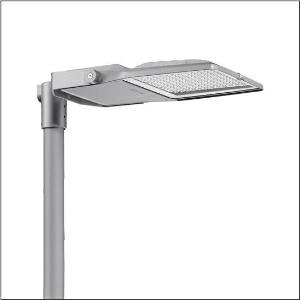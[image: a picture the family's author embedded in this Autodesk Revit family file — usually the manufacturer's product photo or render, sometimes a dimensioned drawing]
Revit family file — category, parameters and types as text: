
# Revit family: floodlight_fl_21_midi___pl43_5xa7786f2a3a_0f3f
name_source: partatom
category: Lighting Fixtures
units: mm (PartAtom-declared; Revit-internal decimal feet)

## family parameters
Cut with Voids When Loaded = No
Host = Face
Light Source = No
Part Type = Normal
Room Calculation Point = No
Round Connector Dimension = Use Diameter
Shared = No

## types (1)
- --- (1 x LED, 36680 lm, 271.6 W, 3000K)
    Apparent Load = 272 VA
    CIE Flux Codes = 27 78 99 100 100
    Color Rendering = 70
    Color Temperature = 3000K
    Default Elevation = 1800 mm
    Description = Floodlight FL 21 midi, floodlight, primary light control with lens, of PMMA, primary optical cover: protective disc, of toughened safety glass, transparent, light distribution: PL43, light emission: direct distribution, installation type: surface-mounted, LED, High Power LED, rated luminous flux: 36.680lm, luminous efficacy: 135lm/W, light colour: 730, colour temperature: 3000K, control gear: ECG Smart Interface, control: flexible luminous flux parameterisation, time-dependent luminous flux control, constant luminous flux control, overheat protection, presetting dimming logarithmic, with terminal, 6-pole, mains connection: 220..240V, AC, 50/60Hz, start of lifetime: 272W, end of service life: 287W, reduction: 123W, luminaire housing, of diecast aluminium, powder-coated, Siteco® metallic grey (DB 702S), corrosivity category C5 mid according to DIN EN ISO 12944, sealing non-destructively replaceable, please order mast flange separately, mast bracket, of steel, galvanised, powder-coated, Siteco® metallic grey (DB 702S), Smart Interface below and above, protection rating (complete): IP66, insulation class (complete): insulation class II (safety insulation), certification: CE, protection symbol: D, impact resistance: IK08, permissible operating ambient temperature: -40..+40°C, permissible operating ambient temperature for outdoor applications: -40..+50°C, standard: DIN EN 12944, LABS conformity tested according to VDMA 24364:2018-05, packaging unit: 1 piece

Light Distribution: PL43
    Height = 76 mm
    Lamp = 1 x LED
    Lamp Light Flux = 36680 lm
    Lamp Power = 271.6 W
    Lamp count = 1
    Length = 657 mm
    Luminous efficacy = 135 lm/W
    Manufacturer = Siteco
    ModVariant = No
    Model = 5XA7786F2A3A
    Number of Poles = 1
    OnlyDefault = Yes
    Power Factor = 1
    Product Name = Floodlight FL 21 midi | PL43
    Product group = floodlight | pylon annexe
    ProductGroupID = 6200
    Protection Class = Protection class II
    Protection Degree = IP 66
    RLX_Detail_Level = 1
    RLX_Emergency_Light_Flux = 0 lm
    RLX_Emergency_Type = 0
    RLX_Emergency_Type_DB = No
    RlxData = <blob elided: 153573 chars, md5=1fc7b9b5>
    Socket = socket
    Standby Power = 0 W
    System Light Flux = 36680 lm
    System Power = 272 W
    Type Comments = factory setting: luminous flux: 100 % | dim-lin: 254 | 620 mA
    Type Image = l_1007123.jpg
    URL = http://relux.com
    VarID = @adj_128283
    Voltage = 0 V
    Weight = 0.00 kg
    Width = 442 mm

## geometry (parser evidence)
native form markers: Blend x4, Sweep x12
no freeform markers — native parametric forms only
